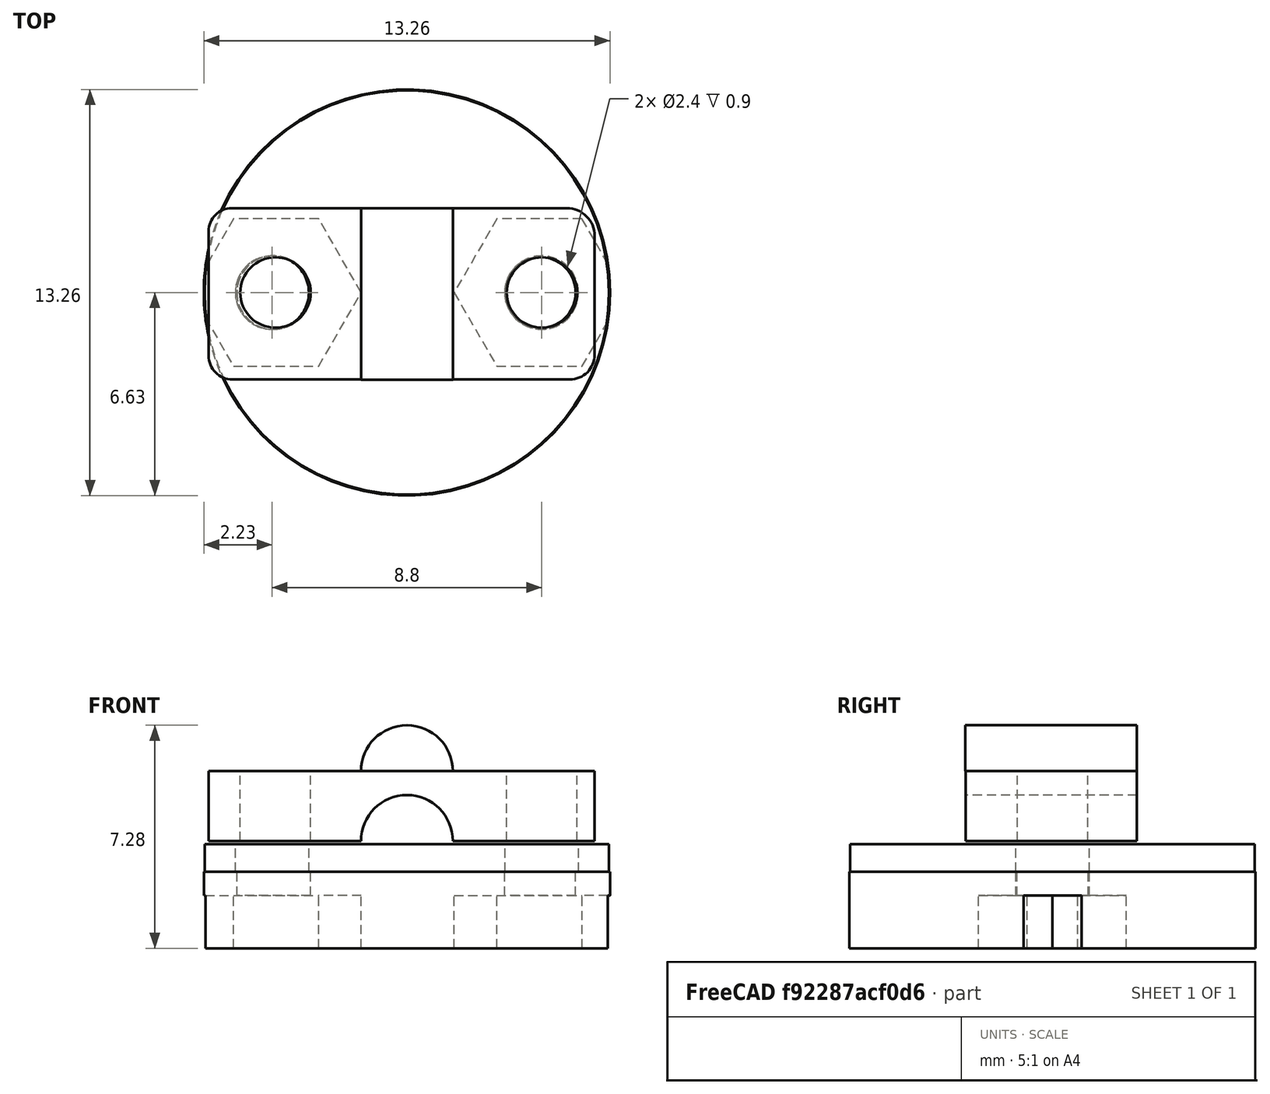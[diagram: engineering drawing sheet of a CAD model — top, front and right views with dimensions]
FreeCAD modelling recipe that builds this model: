
FCSTD DOCUMENT  (FreeCAD 0.16R6706 (Git))
Label: Clamps
License: All rights reserved
LicenseURL: http://en.wikipedia.org/wiki/All_rights_reserved
objects: Part::Cut×7, Part::Cylinder×6, Sketcher::SketchObject×2, Part::Extrusion×2, Part::MultiFuse×2
note: 19 computed .brp shape members not serialized (recipe doc carries the construction recipe); baked Part::Feature solids carry a one-line shape summary decoded from their .brp

FEATURE [Part::Cut] Cut001
FEATURE [Sketcher::SketchObject] Sketch001
  sketch-geometry (7):
    g0: LineSegment StartX=-2.891 StartY=-3.62381e-06 StartZ=0 EndX=-4.28187 EndY=2.40907 EndZ=0
    g1: LineSegment StartX=-4.28187 StartY=2.40907 StartZ=0 EndX=-7.06363 EndY=2.40907 EndZ=0
    g2: LineSegment StartX=-7.06363 StartY=2.40907 StartZ=0 EndX=-8.45451 EndY=3.62381e-06 EndZ=0
    g3: LineSegment StartX=-8.45451 StartY=3.62381e-06 StartZ=0 EndX=-7.06364 EndY=-2.40907 EndZ=0
    g4: LineSegment StartX=-7.06364 StartY=-2.40907 StartZ=0 EndX=-4.28188 EndY=-2.40907 EndZ=0
    g5: LineSegment StartX=-4.28188 StartY=-2.40907 StartZ=0 EndX=-2.891 EndY=-3.62381e-06 EndZ=0
    g6: Circle [constr] CenterX=-5.67276 CenterY=0 CenterZ=0 NormalX=0 NormalY=0 NormalZ=1 Radius=2.78176
  constraints (5):
    c: Coincident(g0,g1)
    c: Coincident(g1,g2)
    c: Coincident(g2,g3)
    c: Coincident(g4,g5)
    c: Coincident(g5,g0)
FEATURE [Part::Extrusion] Extrude
  Base = -> Sketch001
  Dir = (0,0,1.72)
  Placement = pos=(1.4,0,0) rot=(0,0,1;0rad)
  Solid = true
FEATURE [Sketcher::SketchObject] Sketch002
  sketch-geometry (7):
    g0: LineSegment StartX=-2.891 StartY=-3.62381e-06 StartZ=0 EndX=-4.28187 EndY=2.40907 EndZ=0
    g1: LineSegment StartX=-4.28187 StartY=2.40907 StartZ=0 EndX=-7.06363 EndY=2.40907 EndZ=0
    g2: LineSegment StartX=-7.06363 StartY=2.40907 StartZ=0 EndX=-8.45451 EndY=3.62381e-06 EndZ=0
    g3: LineSegment StartX=-8.45451 StartY=3.62381e-06 StartZ=0 EndX=-7.06364 EndY=-2.40907 EndZ=0
    g4: LineSegment StartX=-7.06364 StartY=-2.40907 StartZ=0 EndX=-4.28188 EndY=-2.40907 EndZ=0
    g5: LineSegment StartX=-4.28188 StartY=-2.40907 StartZ=0 EndX=-2.891 EndY=-3.62381e-06 EndZ=0
    g6: Circle [constr] CenterX=-5.67276 CenterY=0 CenterZ=0 NormalX=0 NormalY=0 NormalZ=1 Radius=2.78176
  constraints (5):
    c: Coincident(g0,g1)
    c: Coincident(g1,g2)
    c: Coincident(g2,g3)
    c: Coincident(g4,g5)
    c: Coincident(g5,g0)
FEATURE [Part::Extrusion] Extrude001
  Base = -> Sketch002
  Dir = (0,0,1.72)
  Placement = pos=(10,0,0) rot=(0,0,1;0rad)
  Solid = true
FEATURE [Part::Cut] Cut
  Base = -> Cut001
  Tool = -> Extrude
FEATURE [Part::Cut] Cut002  label="bottom"
  Base = -> Cut
  Placement = pos=(0,-9,2.5) rot=(0,0,1;0rad)
  Tool = -> Extrude001
FEATURE [Part::Cylinder] Cylinder001  label="Cilindro001"
  Angle = 360
  Height = 10
  Placement = pos=(-11.79,0,-4) rot=(0,0,1;0rad)
  Radius = 1.15
FEATURE [Part::Cut] Cut004  label="top"
  Placement = pos=(7.5,-9,5) rot=(0,0,1;0rad)
  Tool = -> Cylinder001
FEATURE [Part::Cylinder] Cylinder  label="Cilindro"
  Angle = 360
  Height = 10
  Placement = pos=(0,-5,5) rot=(1,0,0;1.5708rad)
  Radius = 1.5
FEATURE [Part::Cut] Cut005
  Base = -> Cut004
  Tool = -> Cylinder
FEATURE [Part::Cylinder] Cylinder002  label="Cilindro002"
  Angle = 180
  Height = 5.6
  Placement = pos=(0,-6.25,7.28) rot=(1,0,0;1.5708rad)
  Radius = 1.5
FEATURE [Part::MultiFuse] Fusion  label="top001"
  Placement = pos=(0,0,1) rot=(0,0,1;0rad)
  Shapes = -> [Cylinder002,Cut005]
FEATURE [Part::Cylinder] Cylinder003  label="Cilindro003"
  Angle = 360
  Height = 0.9
  Placement = pos=(0,-9,5) rot=(0,0,1;0rad)
  Radius = 6.6
FEATURE [Part::Cylinder] Cylinder004  label="Cilindro004"
  Angle = 360
  Height = 10
  Placement = pos=(-4.4,-9,1) rot=(0,0,1;0rad)
  Radius = 1.2
FEATURE [Part::Cylinder] Cylinder005  label="Cilindro005"
  Angle = 360
  Height = 10
  Placement = pos=(4.4,-9,1) rot=(0,0,1;0rad)
  Radius = 1.2
FEATURE [Part::Cut] Cut006
  Base = -> Cylinder003
  Tool = -> Cylinder004
FEATURE [Part::Cut] Cut007
  Base = -> Cut006
  Tool = -> Cylinder005
FEATURE [Part::MultiFuse] Fusion001
  Shapes = -> [Cut002,Cut007]
